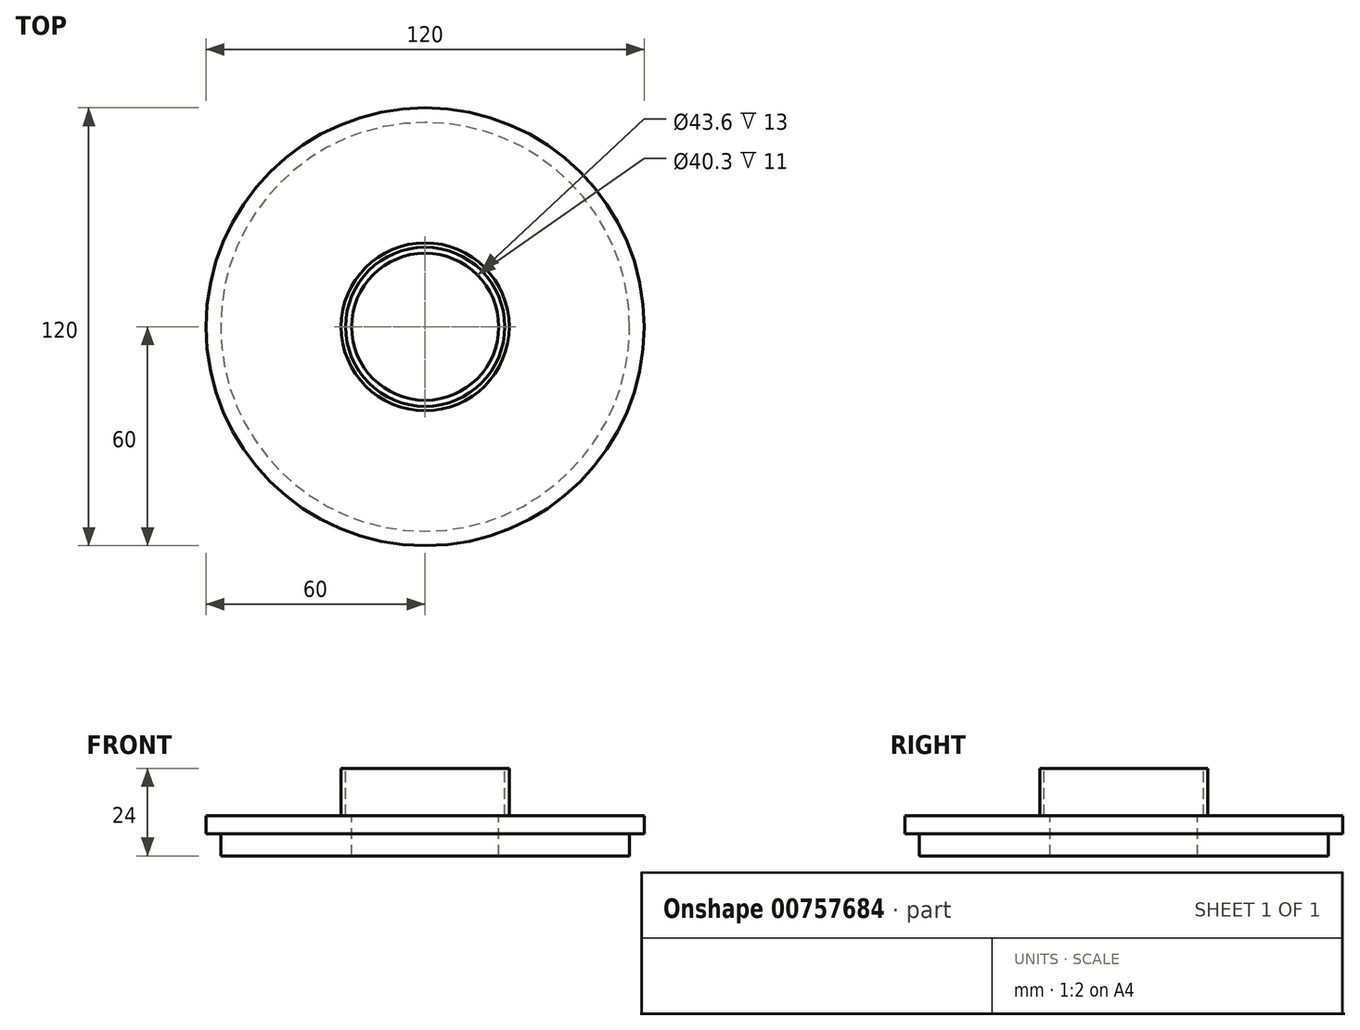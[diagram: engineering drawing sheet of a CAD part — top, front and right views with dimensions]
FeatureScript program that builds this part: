
annotation { "Feature Type Name" : "Feature", "Feature Type Description" : "" }
export const myFeature = defineFeature(function(context is Context, id is Id, definition is map)
    precondition{}
    {
        {
            var Q0;
            Q0=qCreatedBy(makeId("Front.planeOp"),FACE);
            var sketch = newSketch(context, id + "F0", { "sketchPlane" : qUnion([Q0])});
            skLineSegment(sketch, "E0.bottom", {"start": v(0, 0) * mm, "end": v(60, 0) * mm});
            skLineSegment(sketch, "E0.top", {"start": v(0, 5) * mm, "end": v(60, 5) * mm});
            skLineSegment(sketch, "E0.left", {"start": v(0, 0) * mm, "end": v(0, 5) * mm});
            skLineSegment(sketch, "E0.right", {"start": v(60, 0) * mm, "end": v(60, 5) * mm});
            skLineSegment(sketch, "E1.bottom", {"start": v(0, 0) * mm, "end": v(56, 0) * mm});
            skLineSegment(sketch, "E1.top", {"start": v(0, -6) * mm, "end": v(56, -6) * mm});
            skLineSegment(sketch, "E1.left", {"start": v(0, 0) * mm, "end": v(0, -6) * mm});
            skLineSegment(sketch, "E1.right", {"start": v(56, 0) * mm, "end": v(56, -6) * mm});
            skLineSegment(sketch, "E2.bottom", {"start": v(23, 5) * mm, "end": v(24.65, 5) * mm});
            skLineSegment(sketch, "E2.top", {"start": v(23, 18) * mm, "end": v(24.65, 18) * mm});
            skLineSegment(sketch, "E2.left", {"start": v(23, 5) * mm, "end": v(23, 18) * mm});
            skLineSegment(sketch, "E2.right", {"start": v(24.65, 5) * mm, "end": v(24.65, 18) * mm});
            skLineSegment(sketch, "E3.bottom", {"start": v(23, 5) * mm, "end": v(21.8, 5) * mm});
            skLineSegment(sketch, "E3.top", {"start": v(23, 18) * mm, "end": v(21.8, 18) * mm});
            skLineSegment(sketch, "E3.right", {"start": v(21.8, 5) * mm, "end": v(21.8, 18) * mm});
            skLineSegment(sketch, "E4", {"start": v(21.8, 5) * mm, "end": v(21.8, -6) * mm});
            skLineSegment(sketch, "E5.bottom", {"start": v(21.8, 5) * mm, "end": v(20.15, 5) * mm});
            skLineSegment(sketch, "E5.top", {"start": v(21.8, 18) * mm, "end": v(20.15, 18) * mm});
            skLineSegment(sketch, "E5.right", {"start": v(20.15, 5) * mm, "end": v(20.15, 18) * mm});
            skLineSegment(sketch, "E6", {"start": v(20.15, 5) * mm, "end": v(20.15, -6) * mm});
            skSolve(sketch);
        }
        {
            var Q0;
            {var subQ3=sQuery(id+"F0.wireOp",EDGE,"E1.right");Q0=makeQuery(id+"F0.imprint","IMPRINT",FACE,{"disambiguationData":[TD([[makeQuery(id+"F0.imprint","IMPRINT",EDGE,{"derivedFrom":subQ3}),-1.0]])]});}
            var Q1;
            {var subQ2=sQuery(id+"F0.wireOp",EDGE,"E0.right");Q1=makeQuery(id+"F0.imprint","IMPRINT",FACE,{"disambiguationData":[TD([[makeQuery(id+"F0.imprint","IMPRINT",EDGE,{"derivedFrom":subQ2}),1.0]])]});}
            var Q2;
            {var subQ0=sQuery(id+"F0.wireOp",EDGE,"E2.left");Q2=makeQuery(id+"F0.imprint","IMPRINT",FACE,{"disambiguationData":[TD([[makeQuery(id+"F0.imprint","IMPRINT",EDGE,{"derivedFrom":subQ0}),1.0]])]});}
            var Q3;
            {var subQ0=sQuery(id+"F0.wireOp",EDGE,"E4");var subQ1=sQuery(id+"F0.wireOp",EDGE,"E0.bottom");var subQ2=makeQuery(id+"F0.imprint","INTERSECT",VERTEX,{"derivedFrom":[subQ1,subQ0]});Q3=makeQuery(id+"F0.imprint","IMPRINT",FACE,{"disambiguationData":[TD([[makeQuery(id+"F0.imprint","IMPRINT",EDGE,{"disambiguationData":[TD([[subQ2,1.0]])],"derivedFrom":subQ1}),1.0]])]});}
            var Q4;
            {var subQ0=sQuery(id+"F0.wireOp",EDGE,"E4");var subQ1=sQuery(id+"F0.wireOp",EDGE,"E0.bottom");var subQ2=makeQuery(id+"F0.imprint","INTERSECT",VERTEX,{"derivedFrom":[subQ1,subQ0]});Q4=makeQuery(id+"F0.imprint","IMPRINT",FACE,{"disambiguationData":[TD([[makeQuery(id+"F0.imprint","IMPRINT",EDGE,{"disambiguationData":[TD([[subQ2,1.0]])],"derivedFrom":subQ1}),-1.0]])]});}
            var Q5;
            Q5=sQuery(id+"F0.wireOp",EDGE,"E1.left");
            revolve(context, id + "F1", {"surfaceOperationType" : NewSurfaceOperationType.NEW, "entities" : qUnion([Q0, Q1, Q2, Q3, Q4]), "axis" : qUnion([Q5]), "revolveType" : RevolveType.FULL});
        }
    });
